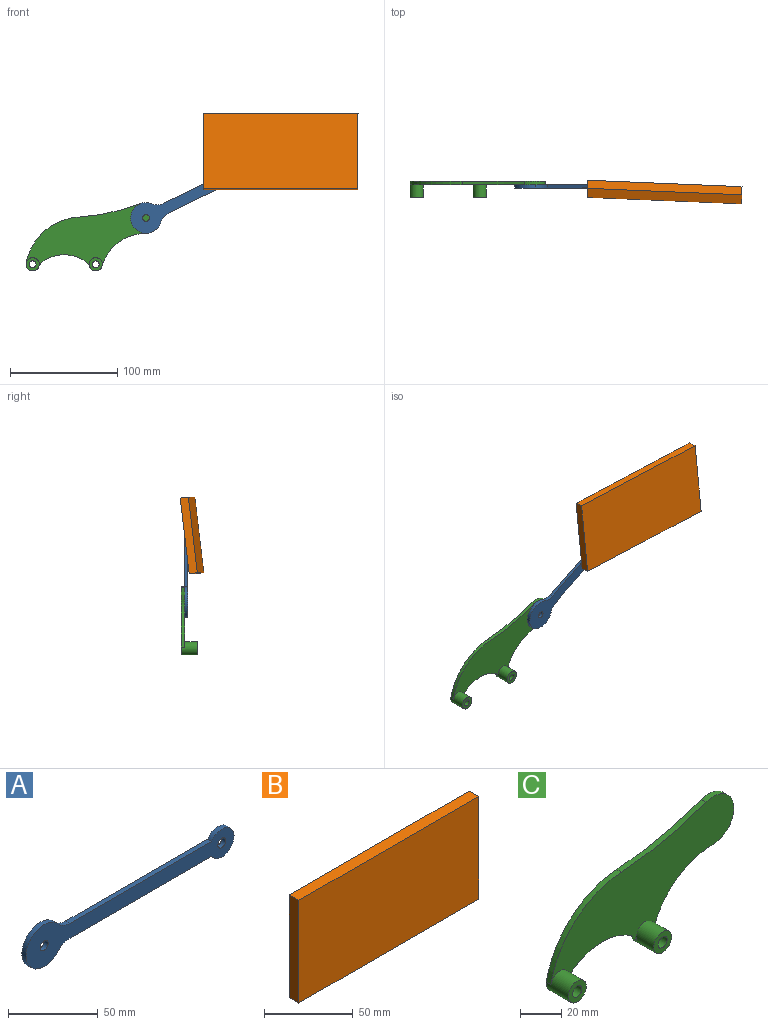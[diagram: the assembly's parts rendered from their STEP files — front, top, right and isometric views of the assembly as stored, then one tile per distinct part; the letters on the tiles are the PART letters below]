
ASSEMBLY  parts=3 mates=2
PART A: 10 faces, bbox 163.5x3.2x28.6 mm
  f0: plane 111.34x3.18mm, normal (0,0,1), area 353.5mm2, adj f3,f4,f5,f9
  f1: cylinder r=14.29mm len=28.58mm, axis (0,-1,0), area 219.8mm2, adj f4,f5,f8,f9
  f2: plane 111.34x3.18mm, normal (0,0,-1), area 353.5mm2, adj f3,f4,f5,f8
  f3: cylinder r=9.53mm len=19.05mm, axis (0,-1,0), area 156mm2, adj f0,f2,f4,f5
  f4: plane 163.51x28.58mm, normal (0,1,0), area 2060.9mm2, adj f0,f1,f2,f3,f6,f7,f8,f9
  f5: plane 163.51x28.58mm, normal (0,-1,0), area 2060.9mm2, adj f0,f1,f2,f3,f6,f7,f8,f9
  f6: cylinder r=3.17mm len=6.35mm, axis (0,-1,0), area 63.3mm2, adj f4,f5
  f7: cylinder r=3.17mm len=6.35mm, axis (0,-1,0), area 63.3mm2, adj f4,f5
  f8: cylinder r=12.7mm len=9.55mm, axis (0,-1,0), area 34.3mm2, adj f1,f2,f4,f5
  f9: cylinder r=12.7mm len=9.55mm, axis (0,-1,0), area 34.3mm2, adj f0,f1,f4,f5
PART B: 6 faces, bbox 143.5x7.6x70.9 mm
  f0: plane 143.51x7.62mm, normal (0,0,-1), area 1093.5mm2, adj f1,f3,f4,f5
  f1: plane 70.87x7.62mm, normal (1,0,0), area 540mm2, adj f0,f2,f4,f5
  f2: plane 143.51x7.62mm, normal (0,0,1), area 1093.5mm2, adj f1,f3,f4,f5
  f3: plane 70.87x7.62mm, normal (-1,0,0), area 540mm2, adj f0,f2,f4,f5
  f4: plane 143.51x70.87mm, normal (0,-1,0), area 10170mm2, adj f0,f1,f2,f3
  f5: plane 143.51x70.87mm, normal (0,1,0), area 10170mm2, adj f0,f1,f2,f3
PART C: 15 faces, bbox 126x15.2x63.6 mm
  f0: plane 125.94x59.62mm, normal (0,-1,0), area 3763.9mm2, adj f1,f2,f3,f4,f5,f6,f7,f13
  f1: cylinder r=34.75mm len=39.8mm, axis (0,1,0), area 134.6mm2, adj f0,f8,f13,f14
  f2: cylinder r=6.17mm len=15.24mm, axis (0,1,0), area 522.5mm2, adj f0,f3,f8,f9,f13
  f3: cylinder r=43.03mm len=40.64mm, axis (0,1,0), area 168.9mm2, adj f0,f2,f4,f8
  f4: cylinder r=14.29mm len=28.58mm, axis (0,1,0), area 158.9mm2, adj f0,f3,f5,f8
  f5: cylinder r=200.67mm len=58.13mm, axis (0,1,0), area 189.5mm2, adj f0,f4,f6,f8
  f6: cylinder r=52.83mm len=48.46mm, axis (0,1,0), area 220.8mm2, adj f0,f5,f7,f8
  f7: cylinder r=6.17mm len=15.24mm, axis (0,1,0), area 526.2mm2, adj f0,f6,f8,f10,f14
  f8: plane 126.05x63.64mm, normal (0,1,0), area 3939.9mm2, adj f1,f2,f3,f4,f5,f6,f7,f11
  f9: plane 12.34x12.34mm, normal (0,-1,0), area 88mm2, adj f2,f12
  f10: plane 12.34x12.34mm, normal (0,-1,0), area 88mm2, adj f7,f11
  f11: cylinder r=3.17mm len=15.24mm, axis (0,-1,0), area 304mm2, adj f8,f10
  f12: cylinder r=3.17mm len=15.24mm, axis (0,-1,0), area 304mm2, adj f8,f9
  f13: cylinder r=10.16mm len=4.78mm, axis (0,1,0), area 19.5mm2, adj f0,f1,f2,f8
  f14: cylinder r=10.16mm len=4.78mm, axis (0,1,0), area 19.5mm2, adj f0,f1,f7,f8
PLACE A rot(axis=(0,-1,0),26.1deg) t=(26.82,-6.35,-29.16)mm
PLACE B rot(axis=(-0.02,-1,0.06),179.9deg) t=(417.53,-10.32,147.64)mm
PLACE C at identity fixed
MATE ball B.f5 <-> A.f3  axis (0.04,0.99,-0.12) through (201.61,-6.35,104.73)mm
MATE revolute A.f1 <-> C.f4  axis (0,-1,0) through (76.2,-3.18,43.18)mm
